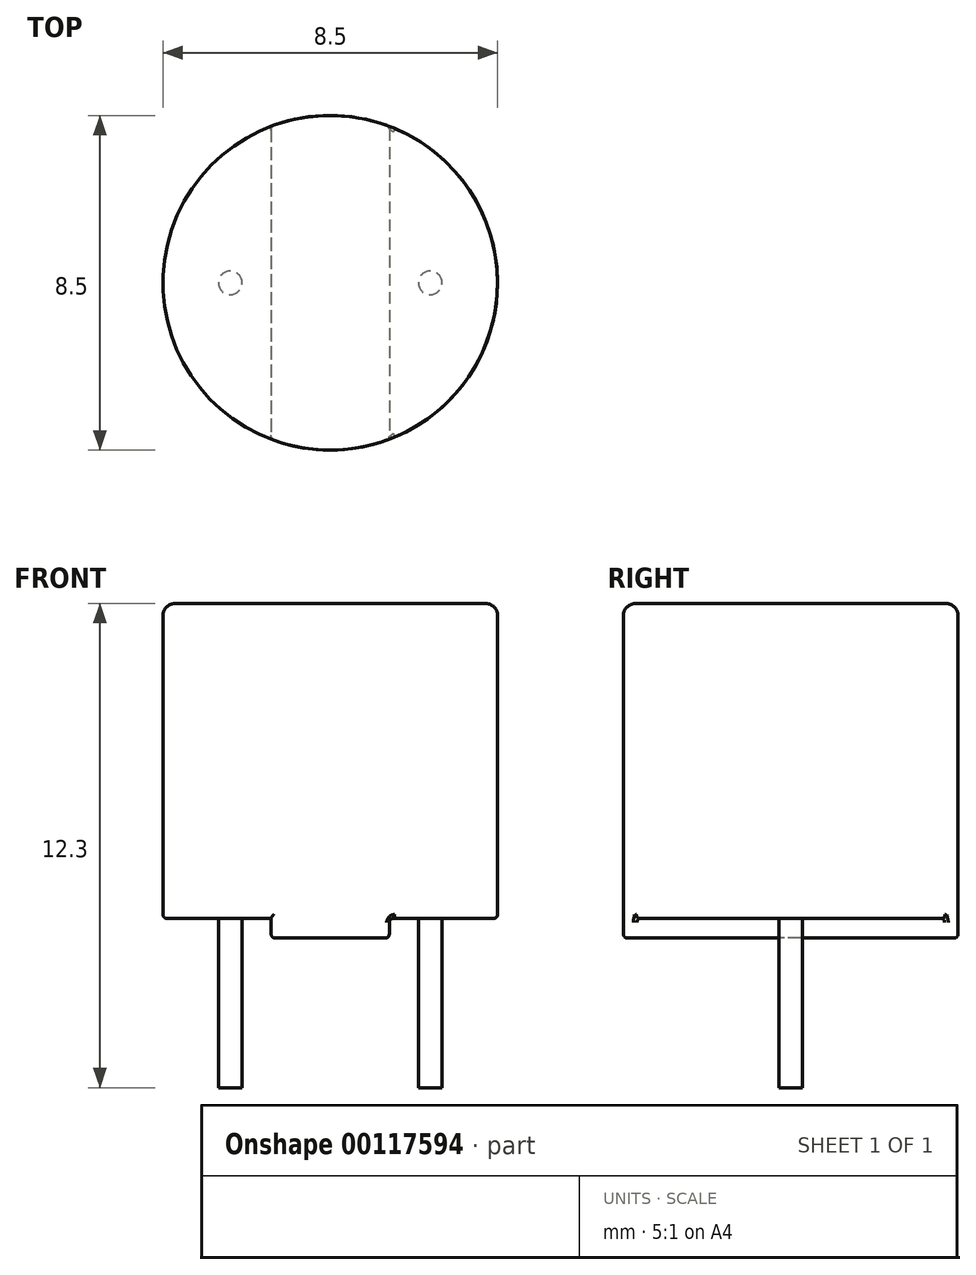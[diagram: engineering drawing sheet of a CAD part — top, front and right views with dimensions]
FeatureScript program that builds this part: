
annotation { "Feature Type Name" : "Feature", "Feature Type Description" : "" }
export const myFeature = defineFeature(function(context is Context, id is Id, definition is map)
    precondition{}
    {
        {
            var Q0;
            Q0=qCreatedBy(makeId("Top.planeOp"),FACE);
            var sketch = newSketch(context, id + "F0", { "sketchPlane" : qUnion([Q0])});
            skCircle(sketch, "E0", {"center": v(0, 0) * mm, "radius": 4.25 * mm});
            skCircle(sketch, "E1", {"center": v(-2.54, 0) * mm, "radius": 0.3 * mm});
            skCircle(sketch, "E2", {"center": v(2.54, 0) * mm, "radius": 0.3 * mm});
            skLineSegment(sketch, "E3", {"start": v(-2.54, 0) * mm, "end": v(2.54, 0) * mm, "construction": true});
            skLineSegment(sketch, "E4.left", {"start": v(-1.5, 3.98) * mm, "end": v(-1.5, -3.98) * mm});
            skLineSegment(sketch, "E4.right", {"start": v(1.5, 3.98) * mm, "end": v(1.5, -3.98) * mm});
            skLineSegment(sketch, "E5", {"start": v(1.5, 0) * mm, "end": v(-1.5, 0) * mm, "construction": true});
            skPoint(sketch, "E6.orphan", {"position": v(-1.5, 4.49) * mm});
            skPoint(sketch, "E7.orphan", {"position": v(1.5, 4.49) * mm});
            skPoint(sketch, "E8.orphan", {"position": v(1.5, -4.49) * mm});
            skPoint(sketch, "E9.orphan", {"position": v(-1.5, -4.49) * mm});
            skSolve(sketch);
        }
        {
            var Q0;
            Q0 = qSketchRegion(id + "F0", true);
            var Q1;
            Q1=makeQuery(id+"F0.imprint","IMPRINT",FACE,{"disambiguationData":[TD([[makeQuery(id+"F0.imprint","IMPRINT",EDGE,{"derivedFrom":sQuery(id+"F0.wireOp",EDGE,"E2")}),-1.0]])]});
            var Q2;
            Q2=makeQuery(id+"F0.imprint","IMPRINT",FACE,{"disambiguationData":[TD([[makeQuery(id+"F0.imprint","IMPRINT",EDGE,{"derivedFrom":sQuery(id+"F0.wireOp",EDGE,"E2")}),1.0]])]});
            var Q3;
            Q3=makeQuery(id+"F0.imprint","IMPRINT",FACE,{"disambiguationData":[TD([[makeQuery(id+"F0.imprint","IMPRINT",EDGE,{"derivedFrom":sQuery(id+"F0.wireOp",EDGE,"E1")}),1.0]])]});
            extrude(context, id + "F5", {"entities" : qUnion([Q0, Q1, Q2, Q3]), "depth" : 8 * mm});
        }
        {
            var Q0;
            {var subQ0=sQuery(id+"F0.wireOp",EDGE,"E4.left");Q0=makeQuery(id+"F0.imprint","IMPRINT",FACE,{"disambiguationData":[TD([[makeQuery(id+"F0.imprint","IMPRINT",EDGE,{"derivedFrom":subQ0}),1.0]])]});}
            extrude(context, id + "F1", {"entities" : qUnion([Q0]), "operationType" : NewBodyOperationType.ADD, "oppositeDirection" : true, "depth" : 0.5 * mm});
        }
        {
            var Q0;
            Q0=makeQuery(id+"F0.imprint","IMPRINT",FACE,{"disambiguationData":[TD([[makeQuery(id+"F0.imprint","IMPRINT",EDGE,{"derivedFrom":sQuery(id+"F0.wireOp",EDGE,"E2")}),1.0]])]});
            var Q1;
            Q1=makeQuery(id+"F0.imprint","IMPRINT",FACE,{"disambiguationData":[TD([[makeQuery(id+"F0.imprint","IMPRINT",EDGE,{"derivedFrom":sQuery(id+"F0.wireOp",EDGE,"E1")}),1.0]])]});
            extrude(context, id + "F2", {"entities" : qUnion([Q0, Q1]), "operationType" : NewBodyOperationType.ADD, "oppositeDirection" : true, "depth" : 4.3 * mm});
        }
        {
            var Q0;
            Q0=makeQuery(id+"F5.opExtrude","CAP_EDGE",EDGE,{"disambiguationData":[OSD([sQuery(id+"F0.wireOp",EDGE,"E0")])],"isStart":false});
            fillet(context, id + "F3", {"entities" : qUnion([Q0]), "radius" : 0.3 * mm, "tangentPropagation" : true, "allowEdgeOverflow" : false});
        }
        {
            var Q0;
            {var subQ1=sQuery(id+"F0.wireOp",EDGE,"E0");var subQ2=sQuery(id+"F0.wireOp",EDGE,"E4.right");Q0=makeQuery(id+"F1.boolean.opBoolean","SPLIT",EDGE,{"disambiguationData":[TD([makeQuery(id+"F1.opExtrude","SWEPT_FACE",FACE,{"disambiguationData":[OSD([subQ2])]})])],"derivedFrom":makeQuery(id+"F5.opExtrude","CAP_EDGE",EDGE,{"disambiguationData":[OSD([subQ1])],"isStart":true})});}
            var Q1;
            {var subQ0=sQuery(id+"F0.wireOp",EDGE,"E0");Q1=makeQuery(id+"F1.opExtrude","CAP_EDGE",EDGE,{"disambiguationData":[OSD([subQ0]),TDD([makeQuery(id+"F0.imprint","IMPRINT",EDGE,{"disambiguationData":[TD([[makeQuery(id+"F0.imprint","INTERSECT",VERTEX,{"disambiguationData":[OD(1.0)],"derivedFrom":[subQ0,sQuery(id+"F0.wireOp",EDGE,"E4.left")]}),-1.0]])],"derivedFrom":subQ0})])],"isStart":false});}
            var Q2;
            Q2=makeQuery(id+"F1.opExtrude","CAP_FACE",FACE,{"disambiguationData":[OSD([sQuery(id+"F0.wireOp",EDGE,"E0"),sQuery(id+"F0.wireOp",EDGE,"E4.left"),sQuery(id+"F0.wireOp",EDGE,"E4.right")])],"isStart":false});
            var Q3;
            {var subQ0=sQuery(id+"F0.wireOp",EDGE,"E4.left");var subQ1=sQuery(id+"F0.wireOp",EDGE,"E0");Q3=makeQuery(id+"F1.boolean.opBoolean","SPLIT",EDGE,{"disambiguationData":[TD([makeQuery(id+"F1.opExtrude","SWEPT_FACE",FACE,{"disambiguationData":[OSD([subQ0])]})])],"derivedFrom":makeQuery(id+"F5.opExtrude","CAP_EDGE",EDGE,{"disambiguationData":[OSD([subQ1])],"isStart":true})});}
            var Q4;
            Q4=makeQuery(id+"F1.opExtrude","SWEPT_FACE",FACE,{"disambiguationData":[OSD([sQuery(id+"F0.wireOp",EDGE,"E4.right")])]});
            var Q5;
            {var subQ0=sQuery(id+"F0.wireOp",EDGE,"E4.left");var subQ1=sQuery(id+"F0.wireOp",EDGE,"E0");Q5=makeQuery(id+"F1.opExtrude","SWEPT_EDGE",EDGE,{"disambiguationData":[OSD([subQ1,subQ0]),TDD([makeQuery(id+"F0.imprint","INTERSECT",VERTEX,{"disambiguationData":[OD(1.0)],"derivedFrom":[subQ1,subQ0]})])]});}
            var Q6;
            {var subQ0=sQuery(id+"F0.wireOp",EDGE,"E4.left");var subQ1=sQuery(id+"F0.wireOp",EDGE,"E0");Q6=makeQuery(id+"F1.opExtrude","SWEPT_EDGE",EDGE,{"disambiguationData":[OSD([subQ1,subQ0]),TDD([makeQuery(id+"F0.imprint","INTERSECT",VERTEX,{"disambiguationData":[OD(0.0)],"derivedFrom":[subQ1,subQ0]})])]});}
            var Q7;
            {var subQ0=sQuery(id+"F0.wireOp",EDGE,"E4.left");var subQ1=sQuery(id+"F0.wireOp",EDGE,"E0");Q7=makeQuery(id+"F1.boolean.opBoolean","MERGE",FACE,{"derivedFrom":[makeQuery(id+"F5.opExtrude","SWEPT_FACE",FACE,{"disambiguationData":[OSD([subQ1])]}),makeQuery(id+"F1.opExtrude","SWEPT_FACE",FACE,{"disambiguationData":[OSD([subQ1]),TDD([makeQuery(id+"F0.imprint","IMPRINT",EDGE,{"disambiguationData":[TD([[makeQuery(id+"F0.imprint","INTERSECT",VERTEX,{"disambiguationData":[OD(0.0)],"derivedFrom":[subQ1,subQ0]}),1.0]])],"derivedFrom":subQ1})])]}),makeQuery(id+"F1.opExtrude","SWEPT_FACE",FACE,{"disambiguationData":[OSD([subQ1]),TDD([makeQuery(id+"F0.imprint","IMPRINT",EDGE,{"disambiguationData":[TD([[makeQuery(id+"F0.imprint","INTERSECT",VERTEX,{"disambiguationData":[OD(1.0)],"derivedFrom":[subQ1,subQ0]}),-1.0]])],"derivedFrom":subQ1})])]})]});}
            fillet(context, id + "F4", {"entities" : qUnion([Q0, Q1, Q2, Q3, Q4, Q5, Q6, Q7]), "radius" : 0.1 * mm, "tangentPropagation" : true, "allowEdgeOverflow" : false});
        }
    });
